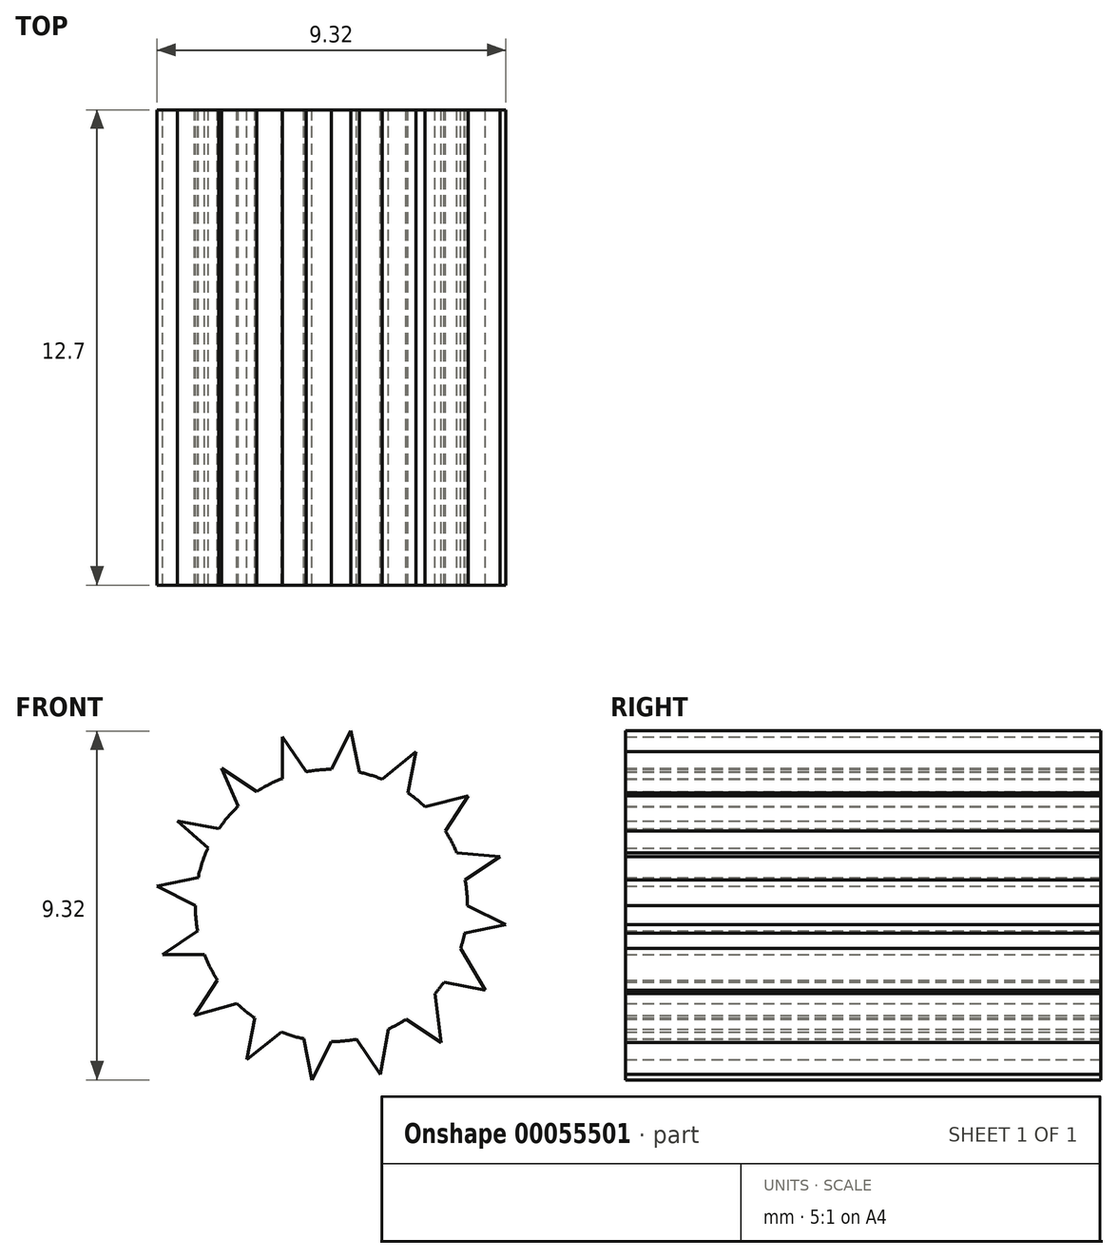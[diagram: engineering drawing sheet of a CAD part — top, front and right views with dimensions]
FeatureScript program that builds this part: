
annotation { "Feature Type Name" : "Feature", "Feature Type Description" : "" }
export const myFeature = defineFeature(function(context is Context, id is Id, definition is map)
    precondition{}
    {
        {
            var Q0;
            Q0=qCreatedBy(makeId("Front.planeOp"),FACE);
            var sketch = newSketch(context, id + "F0", { "sketchPlane" : qUnion([Q0])});
            skCircle(sketch, "E0", {"center": v(0, 0) * mm, "radius": 3.64 * mm});
            skLineSegment(sketch, "E1", {"start": v(0, 3.64) * mm, "end": v(0.51, 4.66) * mm});
            skLineSegment(sketch, "E2", {"start": v(0.51, 4.66) * mm, "end": v(0.74, 3.56) * mm});
            skLineSegment(sketch, "E3", {"start": v(0.74, 3.56) * mm, "end": v(0, 3.64) * mm});
            skLineSegment(sketch, "E4.1.0", {"start": v(-1.3, 4.5) * mm, "end": v(-0.68, 3.57) * mm});
            skLineSegment(sketch, "E4.2.0", {"start": v(-2.93, 3.66) * mm, "end": v(-2, 3.04) * mm});
            skLineSegment(sketch, "E4.3.0", {"start": v(-4.11, 2.26) * mm, "end": v(-3, 2.05) * mm});
            skLineSegment(sketch, "E4.4.0", {"start": v(-4.66, 0.51) * mm, "end": v(-3.56, 0.74) * mm});
            skLineSegment(sketch, "E4.5.0", {"start": v(-4.5, -1.3) * mm, "end": v(-3.57, -0.68) * mm});
            skLineSegment(sketch, "E4.6.0", {"start": v(-3.66, -2.93) * mm, "end": v(-3.04, -2) * mm});
            skLineSegment(sketch, "E4.7.0", {"start": v(-2.26, -4.11) * mm, "end": v(-2.05, -3) * mm});
            skLineSegment(sketch, "E4.8.0", {"start": v(-0.51, -4.66) * mm, "end": v(-0.74, -3.56) * mm});
            skLineSegment(sketch, "E4.9.0", {"start": v(1.3, -4.5) * mm, "end": v(0.68, -3.57) * mm});
            skLineSegment(sketch, "E4.10.0", {"start": v(2.93, -3.66) * mm, "end": v(2, -3.04) * mm});
            skLineSegment(sketch, "E4.11.0", {"start": v(4.11, -2.26) * mm, "end": v(3, -2.05) * mm});
            skLineSegment(sketch, "E4.12.0", {"start": v(4.66, -0.51) * mm, "end": v(3.56, -0.74) * mm});
            skLineSegment(sketch, "E4.13.0", {"start": v(4.5, 1.3) * mm, "end": v(3.57, 0.68) * mm});
            skLineSegment(sketch, "E4.14.0", {"start": v(3.66, 2.93) * mm, "end": v(3.04, 2) * mm});
            skLineSegment(sketch, "E4.15.0", {"start": v(2.26, 4.11) * mm, "end": v(2.05, 3) * mm});
            skLineSegment(sketch, "E5", {"start": v(-1.3, 4.5) * mm, "end": v(-1.3, 3.4) * mm});
            skLineSegment(sketch, "E6", {"start": v(-2.93, 3.66) * mm, "end": v(-2.49, 2.66) * mm});
            skLineSegment(sketch, "E7", {"start": v(-4.11, 2.26) * mm, "end": v(-3.3, 1.54) * mm});
            skLineSegment(sketch, "E8", {"start": v(-4.66, 0.51) * mm, "end": v(-3.64, 0) * mm});
            skLineSegment(sketch, "E9", {"start": v(-4.5, -1.3) * mm, "end": v(-3.4, -1.3) * mm});
            skLineSegment(sketch, "E10", {"start": v(-3.66, -2.93) * mm, "end": v(-2.53, -2.62) * mm});
            skLineSegment(sketch, "E11", {"start": v(-2.26, -4.11) * mm, "end": v(-1.33, -3.38) * mm});
            skLineSegment(sketch, "E12", {"start": v(-0.51, -4.66) * mm, "end": v(0, -3.64) * mm});
            skLineSegment(sketch, "E13", {"start": v(1.3, -4.5) * mm, "end": v(1.52, -3.3) * mm});
            skLineSegment(sketch, "E14", {"start": v(4.5, 1.3) * mm, "end": v(3.35, 1.41) * mm});
            skPoint(sketch, "E14.endSnap0", {"position": v(3.35, 2.46) * mm});
            skLineSegment(sketch, "E15", {"start": v(-0.77, 3.55) * mm, "end": v(-1.3, 3.83) * mm});
            skLineSegment(sketch, "E16", {"start": v(4.11, -2.26) * mm, "end": v(3.45, -1.14) * mm});
            skLineSegment(sketch, "E17", {"start": v(2.93, -3.66) * mm, "end": v(2.77, -2.35) * mm});
            skLineSegment(sketch, "E18", {"start": v(2.26, 4.11) * mm, "end": v(1.36, 3.37) * mm});
            skLineSegment(sketch, "E19", {"start": v(3.66, 2.93) * mm, "end": v(2.5, 2.64) * mm});
            skLineSegment(sketch, "E20", {"start": v(4.66, -0.51) * mm, "end": v(3.64, 0) * mm});
            skSolve(sketch);
        }
        {
            var Q0;
            Q0 = qSketchRegion(id + "F0", true);
            extrude(context, id + "F1", {"entities" : qUnion([Q0]), "depth" : 12.7 * mm});
        }
    });
